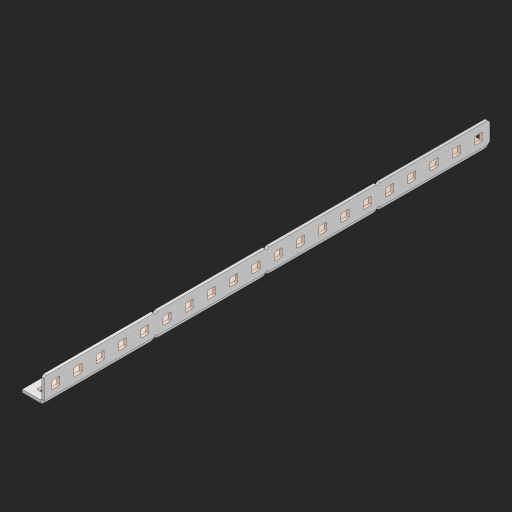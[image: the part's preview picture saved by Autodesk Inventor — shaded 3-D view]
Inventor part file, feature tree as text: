
AUTODESK INVENTOR PART (.ipt)
format: ipt  version: 2023 (Build 270158000, 158)  size: 773,632 bytes
history: native  units: in
note: dims shown in document units (in); Inventor stores cm internally (conversion verified against a paired STEP export)
features: other x45, extrude x39, sheet_metal_op x10, sketch x8, mirror x1, pattern_linear x1, chamfer x1
ambient origin geometry x8: Origin, YZ Plane, XZ Plane, XY Plane, X Axis, Y Axis, Z Axis, Center Point
bodies: Solid1 (feature_tree), Body (feature_tree)
feature tree (105):
  other  "Flange Pattern Plane"
  sheet_metal_op  "Flange Pattern"
  sheet_metal_op  "Body Pattern"
  other  "Arc Length"
  mirror  "Notch Mirror"
  pattern_linear  "Notch Pattern"  Spacing1=0.25in  [1 undecoded]
  chamfer  "End Chamfer"
  extrude  "Half Cut"  Depth=0.0625in
  sketch  "Sketch1"  dims[d0=1.5in]
  other  "Plate1"
  sketch  "Sketch2"  dims[d1=10.0in]
  other  "Plate2"
  sheet_metal_op  "Bend1"
  sheet_metal_op  "Corner1"
  sketch  "Sketch3"  dims[d2=0.0625in]
  other  "Flange Pattern Sketch"
  sketch  "Sketch7"  dims[d3=0.0625in]
  other  "Srf1"
  other  "Srf2"
  sketch  "Sketch8"  dims[d4=0.0312in]
  sketch  "Sketch9"  dims[d5=0.125in]
  other  "Srf91"
  sheet_metal_op  "Body Pattern Sketch"
  other  "Srf92"
  sketch  "Sketch13"  dims[d6=0.0625in]
  sketch  "Sketch14"  dims[d7=0.5in d8=90.0deg d9=0.0312in d10=0.25in d11=0.0625in d12=0.0625in d16=0.182in d17=0.02in d18=0.0625in d19=0.0in d20=0.25in d21=0.25in d46=0.172in d47=1.0in d48=0.0in d49=0.182in d50=0.02in d51=0.25in d52=0.25in d53=0.0625in d54=0.0in d55=0.172in d56=1.0in d57=0.0in d60=7.874in d62=0.5in d63=0.3937in d65=0.5in d85=0.1473in d86=0.1782in d88=0.04in d89=0.0625in d90=0.0in d91=0.04in d92=0.0491in d95=2.5in d96=0.04in d97=0.25in d98=45.0deg d101=0.0in d102=2.497in d131=0.5in d132=7.874in d134=0.5in d139=0.5in]
  other  "Srf856"
  other  "Srf1310"
  other  "Srf1311"
  other  "Srf1312"
  other  "Srf1376"
  other  "Srf1377"
  other  "Srf1728"
  other  "Srf1755"
  other  "Srf1878"
  other  "Srf1879"
  other  "Srf1880"
  other  "Srf1881"
  other  "Srf1882"
  other  "Srf1883"
  other  "Srf1884"
  other  "Srf1885"
  other  "Srf1886"
  other  "Srf1887"
  other  "Srf1888"
  other  "Srf1889"
  other  "Srf1890"
  other  "Srf1891"
  other  "Srf1942"
  other  "Srf1943"
  other  "Srf1944"
  other  "Srf1945"
  other  "Srf1946"
  other  "Srf1947"
  other  "Srf1948"
  other  "Srf1949"
  other  "Srf1950"
  other  "Srf1951"
  other  "Srf1952"
  other  "Srf1953"
  other  "Srf1954"
  other  "Srf1955"
  sheet_metal_op  "Flange Stamp"
  sheet_metal_op  "Flange Circle"
  sheet_metal_op  "Body Stamp"
  sheet_metal_op  "Body Circle"
  sheet_metal_op  "Notch"
  extrude  "ExtrusionSrf2"  Depth=0.0625in
  extrude  "ExtrusionSrf92"  Depth=0.5in
  extrude  "ExtrusionSrf856"  Depth=0.02in
  extrude  "ExtrusionSrf1310"  Depth=0.0625in
  extrude  "ExtrusionSrf1311"  TaperAngle=0.0deg  [1 undecoded]
  extrude  "ExtrusionSrf1312"  Depth=0.5in
  extrude  "ExtrusionSrf1376"  Depth=0.5in
  extrude  "ExtrusionSrf1377"  Depth=0.5in
  extrude  "ExtrusionSrf1728"  Depth=0.5in TaperAngle=0.0deg
  extrude  "ExtrusionSrf1755"  Depth=0.5in
  extrude  "ExtrusionSrf1878"  Depth=0.02in
  extrude  "ExtrusionSrf1879"  Depth=0.5in
  extrude  "ExtrusionSrf1880"  Depth=0.5in
  extrude  "ExtrusionSrf1881"  Depth=0.0625in
  extrude  "ExtrusionSrf1882"  TaperAngle=0.0deg  [1 undecoded]
  extrude  "ExtrusionSrf1883"  Depth=0.5in
  extrude  "ExtrusionSrf1884"  Depth=0.5in TaperAngle=0.0deg
  extrude  "ExtrusionSrf1885"  Depth=0.5in
  extrude  "ExtrusionSrf1886"  Depth=0.5in
  extrude  "ExtrusionSrf1887"  Depth=0.5in
  extrude  "ExtrusionSrf1888"  Depth=0.5in
  extrude  "ExtrusionSrf1889"  Depth=0.5in
  extrude  "ExtrusionSrf1890"  Depth=0.0625in
  extrude  "ExtrusionSrf1891"  TaperAngle=0.0deg  [1 undecoded]
  extrude  "ExtrusionSrf1942"  Depth=0.5in
  extrude  "ExtrusionSrf1943"  Depth=0.5in
  extrude  "ExtrusionSrf1944"  Depth=0.5in
  extrude  "ExtrusionSrf1945"  Depth=0.5in TaperAngle=45.0deg
  extrude  "ExtrusionSrf1946"  TaperAngle=0.0deg  [1 undecoded]
  extrude  "ExtrusionSrf1947"  Depth=0.5in
  extrude  "ExtrusionSrf1948"  Depth=0.5in
  extrude  "ExtrusionSrf1949"  Depth=0.5in
  extrude  "ExtrusionSrf1950"  Depth=0.5in
  extrude  "ExtrusionSrf1951"  Depth=0.5in
  extrude  "ExtrusionSrf1952"  [1 undecoded]
  extrude  "ExtrusionSrf1953"  [1 undecoded]
  extrude  "ExtrusionSrf1954"  [1 undecoded]
  extrude  "ExtrusionSrf1955"  [1 undecoded]
note: 9 required parameter values undecoded (feature->parameter linkage not recoverable at this tier; creation-order binding heuristic only, values carry confidence <= 0.55)
